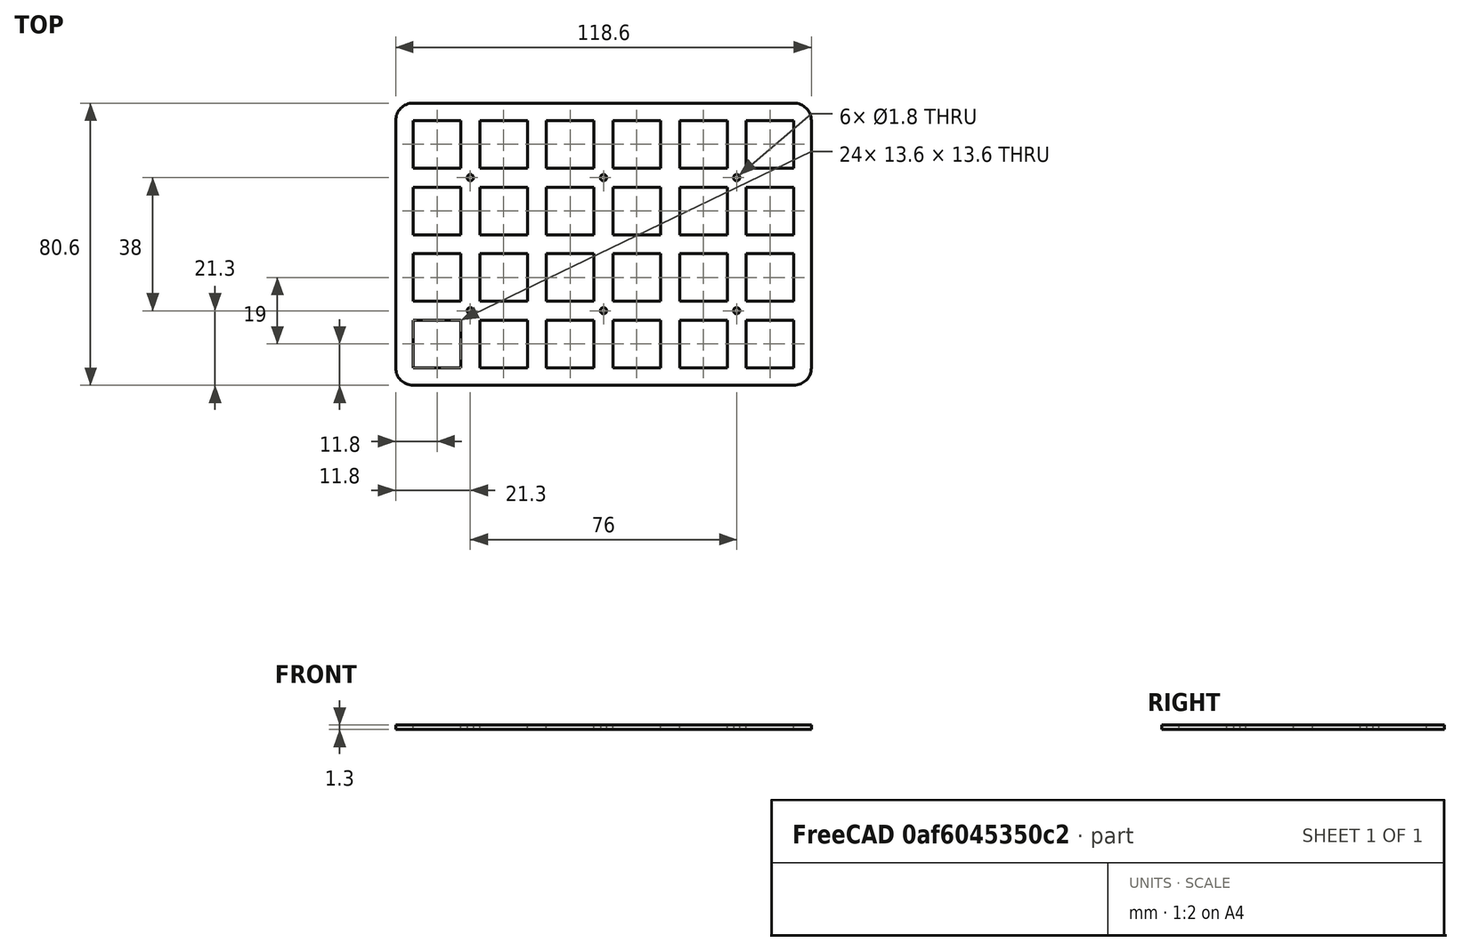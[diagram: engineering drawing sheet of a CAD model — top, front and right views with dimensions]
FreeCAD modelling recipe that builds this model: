
FCSTD DOCUMENT  (FreeCAD 0.18R15860 (Git))
Label: switch mounting plate laser cut size
License: All rights reserved
LicenseURL: http://en.wikipedia.org/wiki/All_rights_reserved
objects: Sketcher::SketchObject×1, PartDesign::Pad×1, PartDesign::Body×1
note: 4 computed .brp shape members not serialized (recipe doc carries the construction recipe); baked Part::Feature solids carry a one-line shape summary decoded from their .brp

FEATURE [Sketcher::SketchObject] Sketch
  MapMode = 5
  Support = -> [XY_Plane]
  sketch-geometry (122):
    g0: LineSegment StartX=0 StartY=0 StartZ=0 EndX=13.6 EndY=0 EndZ=0
    g1: LineSegment StartX=13.6 StartY=0 StartZ=0 EndX=13.6 EndY=13.6 EndZ=0
    g2: LineSegment StartX=13.6 StartY=13.6 StartZ=0 EndX=0 EndY=13.6 EndZ=0
    g3: LineSegment StartX=0 StartY=13.6 StartZ=0 EndX=0 EndY=0 EndZ=0
    g4: LineSegment StartX=19 StartY=0 StartZ=0 EndX=32.6 EndY=0 EndZ=0
    g5: LineSegment StartX=32.6 StartY=0 StartZ=0 EndX=32.6 EndY=13.6 EndZ=0
    g6: LineSegment StartX=32.6 StartY=13.6 StartZ=0 EndX=19 EndY=13.6 EndZ=0
    g7: LineSegment StartX=19 StartY=13.6 StartZ=0 EndX=19 EndY=0 EndZ=0
    g8: LineSegment StartX=38 StartY=0 StartZ=0 EndX=51.6 EndY=0 EndZ=0
    g9: LineSegment StartX=51.6 StartY=0 StartZ=0 EndX=51.6 EndY=13.6 EndZ=0
    g10: LineSegment StartX=51.6 StartY=13.6 StartZ=0 EndX=38 EndY=13.6 EndZ=0
    g11: LineSegment StartX=38 StartY=13.6 StartZ=0 EndX=38 EndY=0 EndZ=0
    g12: LineSegment StartX=57 StartY=0 StartZ=0 EndX=70.6 EndY=0 EndZ=0
    g13: LineSegment StartX=70.6 StartY=0 StartZ=0 EndX=70.6 EndY=13.6 EndZ=0
    g14: LineSegment StartX=70.6 StartY=13.6 StartZ=0 EndX=57 EndY=13.6 EndZ=0
    g15: LineSegment StartX=57 StartY=13.6 StartZ=0 EndX=57 EndY=0 EndZ=0
    g16: LineSegment StartX=76 StartY=0 StartZ=0 EndX=89.6 EndY=0 EndZ=0
    g17: LineSegment StartX=89.6 StartY=0 StartZ=0 EndX=89.6 EndY=13.6 EndZ=0
    g18: LineSegment StartX=89.6 StartY=13.6 StartZ=0 EndX=76 EndY=13.6 EndZ=0
    g19: LineSegment StartX=76 StartY=13.6 StartZ=0 EndX=76 EndY=0 EndZ=0
    g20: LineSegment StartX=95 StartY=0 StartZ=0 EndX=108.6 EndY=0 EndZ=0
    g21: LineSegment StartX=108.6 StartY=0 StartZ=0 EndX=108.6 EndY=13.6 EndZ=0
    g22: LineSegment StartX=108.6 StartY=13.6 StartZ=0 EndX=95 EndY=13.6 EndZ=0
    g23: LineSegment StartX=95 StartY=13.6 StartZ=0 EndX=95 EndY=0 EndZ=0
    g24: LineSegment StartX=0 StartY=-19 StartZ=0 EndX=13.6 EndY=-19 EndZ=0
    g25: LineSegment StartX=13.6 StartY=-19 StartZ=0 EndX=13.6 EndY=-5.4 EndZ=0
    g26: LineSegment StartX=13.6 StartY=-5.4 StartZ=0 EndX=0 EndY=-5.4 EndZ=0
    g27: LineSegment StartX=0 StartY=-5.4 StartZ=0 EndX=0 EndY=-19 EndZ=0
    g28: LineSegment StartX=19 StartY=-19 StartZ=0 EndX=32.6 EndY=-19 EndZ=0
    g29: LineSegment StartX=32.6 StartY=-19 StartZ=0 EndX=32.6 EndY=-5.4 EndZ=0
    g30: LineSegment StartX=32.6 StartY=-5.4 StartZ=0 EndX=19 EndY=-5.4 EndZ=0
    g31: LineSegment StartX=19 StartY=-5.4 StartZ=0 EndX=19 EndY=-19 EndZ=0
    g32: LineSegment StartX=38 StartY=-19 StartZ=0 EndX=51.6 EndY=-19 EndZ=0
    g33: LineSegment StartX=51.6 StartY=-19 StartZ=0 EndX=51.6 EndY=-5.4 EndZ=0
    g34: LineSegment StartX=51.6 StartY=-5.4 StartZ=0 EndX=38 EndY=-5.4 EndZ=0
    g35: LineSegment StartX=38 StartY=-5.4 StartZ=0 EndX=38 EndY=-19 EndZ=0
    g36: LineSegment StartX=57 StartY=-19 StartZ=0 EndX=70.6 EndY=-19 EndZ=0
    g37: LineSegment StartX=70.6 StartY=-19 StartZ=0 EndX=70.6 EndY=-5.4 EndZ=0
    g38: LineSegment StartX=70.6 StartY=-5.4 StartZ=0 EndX=57 EndY=-5.4 EndZ=0
    g39: LineSegment StartX=57 StartY=-5.4 StartZ=0 EndX=57 EndY=-19 EndZ=0
    g40: LineSegment StartX=76 StartY=-19 StartZ=0 EndX=89.6 EndY=-19 EndZ=0
    g41: LineSegment StartX=89.6 StartY=-19 StartZ=0 EndX=89.6 EndY=-5.4 EndZ=0
    g42: LineSegment StartX=89.6 StartY=-5.4 StartZ=0 EndX=76 EndY=-5.4 EndZ=0
    g43: LineSegment StartX=76 StartY=-5.4 StartZ=0 EndX=76 EndY=-19 EndZ=0
    g44: LineSegment StartX=95 StartY=-19 StartZ=0 EndX=108.6 EndY=-19 EndZ=0
    g45: LineSegment StartX=108.6 StartY=-19 StartZ=0 EndX=108.6 EndY=-5.4 EndZ=0
    g46: LineSegment StartX=108.6 StartY=-5.4 StartZ=0 EndX=95 EndY=-5.4 EndZ=0
    g47: LineSegment StartX=95 StartY=-5.4 StartZ=0 EndX=95 EndY=-19 EndZ=0
    g48: LineSegment StartX=0 StartY=-38 StartZ=0 EndX=13.6 EndY=-38 EndZ=0
    g49: LineSegment StartX=13.6 StartY=-38 StartZ=0 EndX=13.6 EndY=-24.4 EndZ=0
    g50: LineSegment StartX=13.6 StartY=-24.4 StartZ=0 EndX=0 EndY=-24.4 EndZ=0
    g51: LineSegment StartX=0 StartY=-24.4 StartZ=0 EndX=0 EndY=-38 EndZ=0
    g52: LineSegment StartX=19 StartY=-38 StartZ=0 EndX=32.6 EndY=-38 EndZ=0
    g53: LineSegment StartX=32.6 StartY=-38 StartZ=0 EndX=32.6 EndY=-24.4 EndZ=0
    g54: LineSegment StartX=32.6 StartY=-24.4 StartZ=0 EndX=19 EndY=-24.4 EndZ=0
    g55: LineSegment StartX=19 StartY=-24.4 StartZ=0 EndX=19 EndY=-38 EndZ=0
    g56: LineSegment StartX=38 StartY=-38 StartZ=0 EndX=51.6 EndY=-38 EndZ=0
    g57: LineSegment StartX=51.6 StartY=-38 StartZ=0 EndX=51.6 EndY=-24.4 EndZ=0
    g58: LineSegment StartX=51.6 StartY=-24.4 StartZ=0 EndX=38 EndY=-24.4 EndZ=0
    g59: LineSegment StartX=38 StartY=-24.4 StartZ=0 EndX=38 EndY=-38 EndZ=0
    g60: LineSegment StartX=57 StartY=-38 StartZ=0 EndX=70.6 EndY=-38 EndZ=0
    g61: LineSegment StartX=70.6 StartY=-38 StartZ=0 EndX=70.6 EndY=-24.4 EndZ=0
    g62: LineSegment StartX=70.6 StartY=-24.4 StartZ=0 EndX=57 EndY=-24.4 EndZ=0
    g63: LineSegment StartX=57 StartY=-24.4 StartZ=0 EndX=57 EndY=-38 EndZ=0
    g64: LineSegment StartX=76 StartY=-38 StartZ=0 EndX=89.6 EndY=-38 EndZ=0
    g65: LineSegment StartX=89.6 StartY=-38 StartZ=0 EndX=89.6 EndY=-24.4 EndZ=0
    g66: LineSegment StartX=89.6 StartY=-24.4 StartZ=0 EndX=76 EndY=-24.4 EndZ=0
    g67: LineSegment StartX=76 StartY=-24.4 StartZ=0 EndX=76 EndY=-38 EndZ=0
    g68: LineSegment StartX=95 StartY=-38 StartZ=0 EndX=108.6 EndY=-38 EndZ=0
    g69: LineSegment StartX=108.6 StartY=-38 StartZ=0 EndX=108.6 EndY=-24.4 EndZ=0
    g70: LineSegment StartX=108.6 StartY=-24.4 StartZ=0 EndX=95 EndY=-24.4 EndZ=0
    g71: LineSegment StartX=95 StartY=-24.4 StartZ=0 EndX=95 EndY=-38 EndZ=0
    g72: LineSegment StartX=0 StartY=-57 StartZ=0 EndX=13.6 EndY=-57 EndZ=0
    g73: LineSegment StartX=13.6 StartY=-57 StartZ=0 EndX=13.6 EndY=-43.4 EndZ=0
    g74: LineSegment StartX=13.6 StartY=-43.4 StartZ=0 EndX=0 EndY=-43.4 EndZ=0
    g75: LineSegment StartX=0 StartY=-43.4 StartZ=0 EndX=0 EndY=-57 EndZ=0
    g76: LineSegment StartX=19 StartY=-57 StartZ=0 EndX=32.6 EndY=-57 EndZ=0
    g77: LineSegment StartX=32.6 StartY=-57 StartZ=0 EndX=32.6 EndY=-43.4 EndZ=0
    g78: LineSegment StartX=32.6 StartY=-43.4 StartZ=0 EndX=19 EndY=-43.4 EndZ=0
    g79: LineSegment StartX=19 StartY=-43.4 StartZ=0 EndX=19 EndY=-57 EndZ=0
    g80: LineSegment StartX=38 StartY=-57 StartZ=0 EndX=51.6 EndY=-57 EndZ=0
    g81: LineSegment StartX=51.6 StartY=-57 StartZ=0 EndX=51.6 EndY=-43.4 EndZ=0
    g82: LineSegment StartX=51.6 StartY=-43.4 StartZ=0 EndX=38 EndY=-43.4 EndZ=0
    g83: LineSegment StartX=38 StartY=-43.4 StartZ=0 EndX=38 EndY=-57 EndZ=0
    g84: LineSegment StartX=57 StartY=-57 StartZ=0 EndX=70.6 EndY=-57 EndZ=0
    g85: LineSegment StartX=70.6 StartY=-57 StartZ=0 EndX=70.6 EndY=-43.4 EndZ=0
    g86: LineSegment StartX=70.6 StartY=-43.4 StartZ=0 EndX=57 EndY=-43.4 EndZ=0
    g87: LineSegment StartX=57 StartY=-43.4 StartZ=0 EndX=57 EndY=-57 EndZ=0
    g88: LineSegment StartX=76 StartY=-57 StartZ=0 EndX=89.6 EndY=-57 EndZ=0
    g89: LineSegment StartX=89.6 StartY=-57 StartZ=0 EndX=89.6 EndY=-43.4 EndZ=0
    g90: LineSegment StartX=89.6 StartY=-43.4 StartZ=0 EndX=76 EndY=-43.4 EndZ=0
    g91: LineSegment StartX=76 StartY=-43.4 StartZ=0 EndX=76 EndY=-57 EndZ=0
    g92: LineSegment StartX=95 StartY=-57 StartZ=0 EndX=108.6 EndY=-57 EndZ=0
    g93: LineSegment StartX=108.6 StartY=-57 StartZ=0 EndX=108.6 EndY=-43.4 EndZ=0
    g94: LineSegment StartX=108.6 StartY=-43.4 StartZ=0 EndX=95 EndY=-43.4 EndZ=0
    g95: LineSegment StartX=95 StartY=-43.4 StartZ=0 EndX=95 EndY=-57 EndZ=0
    g96: LineSegment [constr] StartX=13.6 StartY=-43.4 StartZ=0 EndX=19 EndY=-38 EndZ=0
    g97: LineSegment [constr] StartX=13.6 StartY=-38 StartZ=0 EndX=19 EndY=-43.4 EndZ=0
    g98: LineSegment [constr] StartX=51.6 StartY=-38 StartZ=0 EndX=57 EndY=-43.4 EndZ=0
    g99: LineSegment [constr] StartX=51.6 StartY=-43.4 StartZ=0 EndX=57 EndY=-38 EndZ=0
    g100: LineSegment [constr] StartX=89.6 StartY=-43.4 StartZ=0 EndX=95 EndY=-38 EndZ=0
    g101: LineSegment [constr] StartX=89.6 StartY=-38 StartZ=0 EndX=95 EndY=-43.4 EndZ=0
    g102: Circle CenterX=92.3 CenterY=-40.7 CenterZ=0 NormalX=0 NormalY=0 NormalZ=1 AngleXU=0 Radius=0.9
    g103: Circle CenterX=54.3 CenterY=-40.7 CenterZ=0 NormalX=0 NormalY=0 NormalZ=1 AngleXU=0 Radius=0.9
    g104: Circle CenterX=16.3 CenterY=-40.7 CenterZ=0 NormalX=0 NormalY=0 NormalZ=1 AngleXU=0 Radius=0.9
    g105: LineSegment [constr] StartX=13.6 StartY=-5.4 StartZ=0 EndX=19 EndY=0 EndZ=0
    g106: LineSegment [constr] StartX=13.6 StartY=0 StartZ=0 EndX=19 EndY=-5.4 EndZ=0
    g107: LineSegment [constr] StartX=51.6 StartY=0 StartZ=0 EndX=57 EndY=-5.4 EndZ=0
    g108: LineSegment [constr] StartX=51.6 StartY=-5.4 StartZ=0 EndX=57 EndY=0 EndZ=0
    g109: LineSegment [constr] StartX=89.6 StartY=0 StartZ=0 EndX=95 EndY=-5.4 EndZ=0
    g110: LineSegment [constr] StartX=89.6 StartY=-5.4 StartZ=0 EndX=95 EndY=0 EndZ=0
    g111: Circle CenterX=16.3 CenterY=-2.7 CenterZ=0 NormalX=0 NormalY=0 NormalZ=1 AngleXU=0 Radius=0.9
    g112: Circle CenterX=54.3 CenterY=-2.7 CenterZ=0 NormalX=0 NormalY=0 NormalZ=1 AngleXU=0 Radius=0.9
    g113: Circle CenterX=92.3 CenterY=-2.7 CenterZ=0 NormalX=0 NormalY=0 NormalZ=1 AngleXU=0 Radius=0.9
    g114: ArcOfCircle CenterX=0 CenterY=13.6 CenterZ=0 NormalX=0 NormalY=0 NormalZ=1 AngleXU=0 Radius=5 StartAngle=1.5708 EndAngle=3.14159
    g115: ArcOfCircle CenterX=108.6 CenterY=13.6 CenterZ=0 NormalX=0 NormalY=0 NormalZ=1 AngleXU=0 Radius=5 StartAngle=0 EndAngle=1.5708
    g116: ArcOfCircle CenterX=108.6 CenterY=-57 CenterZ=0 NormalX=0 NormalY=0 NormalZ=1 AngleXU=0 Radius=5 StartAngle=4.71239 EndAngle=6.28319
    g117: ArcOfCircle CenterX=0 CenterY=-57 CenterZ=0 NormalX=0 NormalY=0 NormalZ=1 AngleXU=0 Radius=5 StartAngle=3.14159 EndAngle=4.71239
    g118: LineSegment StartX=-9e-16 StartY=-62 StartZ=0 EndX=108.6 EndY=-62 EndZ=0
    g119: LineSegment StartX=113.6 StartY=-57 StartZ=0 EndX=113.6 EndY=13.6 EndZ=0
    g120: LineSegment StartX=108.6 StartY=18.6 StartZ=0 EndX=0 EndY=18.6 EndZ=0
    g121: LineSegment StartX=-5 StartY=13.6 StartZ=0 EndX=-5 EndY=-57 EndZ=0
  constraints (355):
    c: Coincident(g0,g1)
    c: Coincident(g1,g2)
    c: Coincident(g2,g3)
    c: Coincident(g3,g0)
    c: Horizontal(g0)
    c: Horizontal(g2)
    c: Vertical(g1)
    c: Vertical(g3)
    c: Coincident(g0,g-1)
    c: Distance(g2) = 13.6
    c: Distance(g3) = 13.6
    c: Coincident(g4,g5)
    c: Coincident(g5,g6)
    c: Coincident(g6,g7)
    c: Coincident(g7,g4)
    c: Horizontal(g4)
    c: Horizontal(g6)
    c: Vertical(g5)
    c: Vertical(g7)
    c: PointOnObject(g4,g-1)
    c: Coincident(g8,g9)
    c: Coincident(g9,g10)
    c: Coincident(g10,g11)
    c: Coincident(g11,g8)
    c: Horizontal(g8)
    c: Horizontal(g10)
    c: Vertical(g9)
    c: Vertical(g11)
    c: PointOnObject(g8,g-1)
    c: Coincident(g12,g13)
    c: Coincident(g13,g14)
    c: Coincident(g14,g15)
    c: Coincident(g15,g12)
    c: Horizontal(g12)
    c: Horizontal(g14)
    c: Vertical(g13)
    c: Vertical(g15)
    c: PointOnObject(g12,g-1)
    c: Coincident(g16,g17)
    c: Coincident(g17,g18)
    c: Coincident(g18,g19)
    c: Coincident(g19,g16)
    c: Horizontal(g16)
    c: Horizontal(g18)
    c: Vertical(g17)
    c: Vertical(g19)
    c: PointOnObject(g16,g-1)
    c: Coincident(g20,g21)
    c: Coincident(g21,g22)
    c: Coincident(g22,g23)
    c: Coincident(g23,g20)
    c: Horizontal(g20)
    c: Horizontal(g22)
    c: Vertical(g21)
    c: Vertical(g23)
    c: PointOnObject(g20,g-1)
    c: Distance(g7) = 13.6
    c: Distance(g6) = 13.6
    c: Distance(g0,g4) = 19
    c: Distance(g10) = 13.6
    c: Distance(g11) = 13.6
    c: Distance(g8,g4) = 19
    c: Distance(g15) = 13.6
    c: Distance(g14) = 13.6
    c: Distance(g12,g8) = 19
    c: Distance(g19) = 13.6
    c: Distance(g18) = 13.6
    c: Distance(g16,g12) = 19
    c: Distance(g23) = 13.6
    c: Distance(g22) = 13.6
    c: Distance(g20,g16) = 19
    c: Coincident(g24,g25)
    c: Coincident(g25,g26)
    c: Coincident(g26,g27)
    c: Coincident(g27,g24)
    c: Horizontal(g24)
    c: Horizontal(g26)
    c: Vertical(g25)
    c: Vertical(g27)
    c: Equal(g2,g26) = 13.8
    c: Equal(g3,g27) = 13.8
    c: Coincident(g28,g29)
    c: Coincident(g29,g30)
    c: Coincident(g30,g31)
    c: Coincident(g31,g28)
    c: Horizontal(g28)
    c: Horizontal(g30)
    c: Vertical(g29)
    c: Vertical(g31)
    c: Coincident(g32,g33)
    c: Coincident(g33,g34)
    c: Coincident(g34,g35)
    c: Coincident(g35,g32)
    c: Horizontal(g32)
    c: Horizontal(g34)
    c: Vertical(g33)
    c: Vertical(g35)
    c: Coincident(g36,g37)
    c: Coincident(g37,g38)
    c: Coincident(g38,g39)
    c: Coincident(g39,g36)
    c: Horizontal(g36)
    c: Horizontal(g38)
    c: Vertical(g37)
    c: Vertical(g39)
    c: Coincident(g40,g41)
    c: Coincident(g41,g42)
    c: Coincident(g42,g43)
    c: Coincident(g43,g40)
    c: Horizontal(g40)
    c: Horizontal(g42)
    c: Vertical(g41)
    c: Vertical(g43)
    c: Coincident(g44,g45)
    c: Coincident(g45,g46)
    c: Coincident(g46,g47)
    c: Coincident(g47,g44)
    c: Horizontal(g44)
    c: Horizontal(g46)
    c: Vertical(g45)
    c: Vertical(g47)
    c: Equal(g7,g31) = 13.8
    c: Equal(g6,g30) = 13.8
    c: Distance(g24,g28) = 19
    c: Equal(g10,g34) = 13.8
    c: Equal(g11,g35) = 13.8
    c: Distance(g32,g28) = 19
    c: Equal(g15,g39) = 13.8
    c: Equal(g14,g38) = 13.8
    c: Distance(g36,g32) = 19
    c: Equal(g19,g43) = 13.8
    c: Equal(g18,g42) = 13.8
    c: Distance(g40,g36) = 19
    c: Equal(g23,g47) = 13.8
    c: Equal(g22,g46) = 13.8
    c: Distance(g44,g40) = 19
    c: Horizontal(g26,g30)
    c: Horizontal(g29,g34)
    c: Horizontal(g33,g38)
    c: Horizontal(g37,g42)
    c: Horizontal(g41,g46)
    c: PointOnObject(g26,g-2)
    c: Distance(g26,g2) = 19
    c: Coincident(g48,g49)
    c: Coincident(g49,g50)
    c: Coincident(g50,g51)
    c: Coincident(g51,g48)
    c: Horizontal(g48)
    c: Horizontal(g50)
    c: Vertical(g49)
    c: Vertical(g51)
    c: Coincident(g52,g53)
    c: Coincident(g53,g54)
    c: Coincident(g54,g55)
    c: Coincident(g55,g52)
    c: Horizontal(g52)
    c: Horizontal(g54)
    c: Vertical(g53)
    c: Vertical(g55)
    c: Coincident(g56,g57)
    c: Coincident(g57,g58)
    c: Coincident(g58,g59)
    c: Coincident(g59,g56)
    c: Horizontal(g56)
    c: Horizontal(g58)
    c: Vertical(g57)
    c: Vertical(g59)
    c: Coincident(g60,g61)
    c: Coincident(g61,g62)
    c: Coincident(g62,g63)
    c: Coincident(g63,g60)
    c: Horizontal(g60)
    c: Horizontal(g62)
    c: Vertical(g61)
    c: Vertical(g63)
    c: Coincident(g64,g65)
    c: Coincident(g65,g66)
    c: Coincident(g66,g67)
    c: Coincident(g67,g64)
    c: Horizontal(g64)
    c: Horizontal(g66)
    c: Vertical(g65)
    c: Vertical(g67)
    c: Coincident(g68,g69)
    c: Coincident(g69,g70)
    c: Coincident(g70,g71)
    c: Coincident(g71,g68)
    c: Horizontal(g68)
    c: Horizontal(g70)
    c: Vertical(g69)
    c: Vertical(g71)
    c: Distance(g48,g52) = 19
    c: Distance(g56,g52) = 19
    c: Distance(g60,g56) = 19
    c: Distance(g64,g60) = 19
    c: Distance(g68,g64) = 19
    c: Horizontal(g50,g54)
    c: Horizontal(g53,g58)
    c: Horizontal(g57,g62)
    c: Horizontal(g61,g66)
    c: Horizontal(g65,g70)
    c: PointOnObject(g50,g-2)
    c: Distance(g50,g26) = 19
    c: Distance(g51) = 13.6
    c: Horizontal(g52,g48)
    c: Horizontal(g52,g56)
    c: Horizontal(g56,g60)
    c: Horizontal(g60,g64)
    c: Horizontal(g64,g68)
    c: Distance(g58) = 13.6
    c: Distance(g54) = 13.6
    c: Distance(g62) = 13.6
    c: Distance(g66) = 13.6
    c: Distance(g70) = 13.6
    c: Distance(g50) = 13.6
    c: Coincident(g72,g73)
    c: Coincident(g73,g74)
    c: Coincident(g74,g75)
    c: Coincident(g75,g72)
    c: Horizontal(g72)
    c: Horizontal(g74)
    c: Vertical(g73)
    c: Vertical(g75)
    c: Coincident(g76,g77)
    c: Coincident(g77,g78)
    c: Coincident(g78,g79)
    c: Coincident(g79,g76)
    c: Horizontal(g76)
    c: Horizontal(g78)
    c: Vertical(g77)
    c: Vertical(g79)
    c: Coincident(g80,g81)
    c: Coincident(g81,g82)
    c: Coincident(g82,g83)
    c: Coincident(g83,g80)
    c: Horizontal(g80)
    c: Horizontal(g82)
    c: Vertical(g81)
    c: Vertical(g83)
    c: Coincident(g84,g85)
    c: Coincident(g85,g86)
    c: Coincident(g86,g87)
    c: Coincident(g87,g84)
    c: Horizontal(g84)
    c: Horizontal(g86)
    c: Vertical(g85)
    c: Vertical(g87)
    c: Coincident(g88,g89)
    c: Coincident(g89,g90)
    c: Coincident(g90,g91)
    c: Coincident(g91,g88)
    c: Horizontal(g88)
    c: Horizontal(g90)
    c: Vertical(g89)
    c: Vertical(g91)
    c: Coincident(g92,g93)
    c: Coincident(g93,g94)
    c: Coincident(g94,g95)
    c: Coincident(g95,g92)
    c: Horizontal(g92)
    c: Horizontal(g94)
    c: Vertical(g93)
    c: Vertical(g95)
    c: Distance(g72,g76) = 19
    c: Distance(g80,g76) = 19
    c: Distance(g84,g80) = 19
    c: Distance(g88,g84) = 19
    c: Distance(g92,g88) = 19
    c: Horizontal(g74,g78)
    c: Horizontal(g77,g82)
    c: Horizontal(g81,g86)
    c: Horizontal(g85,g90)
    c: Horizontal(g89,g94)
    c: Equal(g51,g75) = 13.8
    c: Horizontal(g76,g72)
    c: Horizontal(g76,g80)
    c: Horizontal(g80,g84)
    c: Horizontal(g84,g88)
    c: Horizontal(g88,g92)
    c: Equal(g58,g82) = 13.8
    c: Equal(g54,g78) = 13.8
    c: Equal(g62,g86) = 13.8
    c: Equal(g66,g90) = 13.8
    c: Equal(g70,g94) = 13.8
    c: Equal(g50,g74) = 13.8
    c: PointOnObject(g74,g-2)
    c: Distance(g74,g50) = 19
    c: Coincident(g96,g73)
    c: Coincident(g96,g52)
    c: Coincident(g97,g48)
    c: Coincident(g97,g78)
    c: Coincident(g98,g56)
    c: Coincident(g98,g86)
    c: Coincident(g99,g81)
    c: Coincident(g99,g60)
    c: Coincident(g100,g89)
    c: Coincident(g100,g68)
    c: Coincident(g101,g64)
    c: Coincident(g101,g94)
    c: PointOnObject(g102,g100)
    c: PointOnObject(g103,g99)
    c: PointOnObject(g104,g96)
    c: Diameter(g104) = 1.8
    c: Diameter(g103) = 1.8
    c: Diameter(g102) = 1.8
    c: PointOnObject(g103,g98)
    c: PointOnObject(g104,g97)
    c: PointOnObject(g102,g101)
    c: Coincident(g105,g25)
    c: Coincident(g105,g4)
    c: Coincident(g106,g0)
    c: Coincident(g106,g30)
    c: Coincident(g107,g8)
    c: Coincident(g107,g38)
    c: Coincident(g108,g33)
    c: Coincident(g108,g12)
    c: Coincident(g109,g16)
    c: Coincident(g109,g46)
    c: Coincident(g110,g41)
    c: Coincident(g110,g20)
    c: PointOnObject(g111,g105)
    c: PointOnObject(g112,g108)
    c: PointOnObject(g113,g110)
    c: Diameter(g111) = 1.8
    c: Diameter(g112) = 1.8
    c: Diameter(g113) = 1.8
    c: PointOnObject(g111,g106)
    c: PointOnObject(g112,g107)
    c: PointOnObject(g113,g109)
    c: Coincident(g114,g2)
    c: PointOnObject(g114,g-2)
    c: Horizontal(g114,g2)
    c: Coincident(g115,g21)
    c: Vertical(g115,g21)
    c: Horizontal(g21,g22)
    c: Horizontal(g22,g115)
    c: Horizontal(g115,g115)
    c: Radius(g115) = 5
    c: Coincident(g116,g92)
    c: Horizontal(g116,g92)
    c: Vertical(g92,g116)
    c: Coincident(g117,g72)
    c: PointOnObject(g117,g-2)
    c: Horizontal(g117,g72)
    c: Radius(g117) = 5
    c: Coincident(g118,g117)
    c: Horizontal(g118)
    c: Coincident(g116,g118)
    c: Coincident(g119,g116)
    c: Coincident(g119,g115)
    c: Coincident(g120,g115)
    c: Coincident(g120,g114)
    c: Horizontal(g120)
    c: Coincident(g121,g114)
    c: Coincident(g121,g117)
FEATURE [PartDesign::Pad] Pad
  Length = 1.3
  Length2 = 100
  Profile = -> Sketch
  Type = 0
FEATURE [PartDesign::Body] Body
  Group = -> [Sketch,Pad]
  Origin = -> Origin
  Tip = -> Pad
